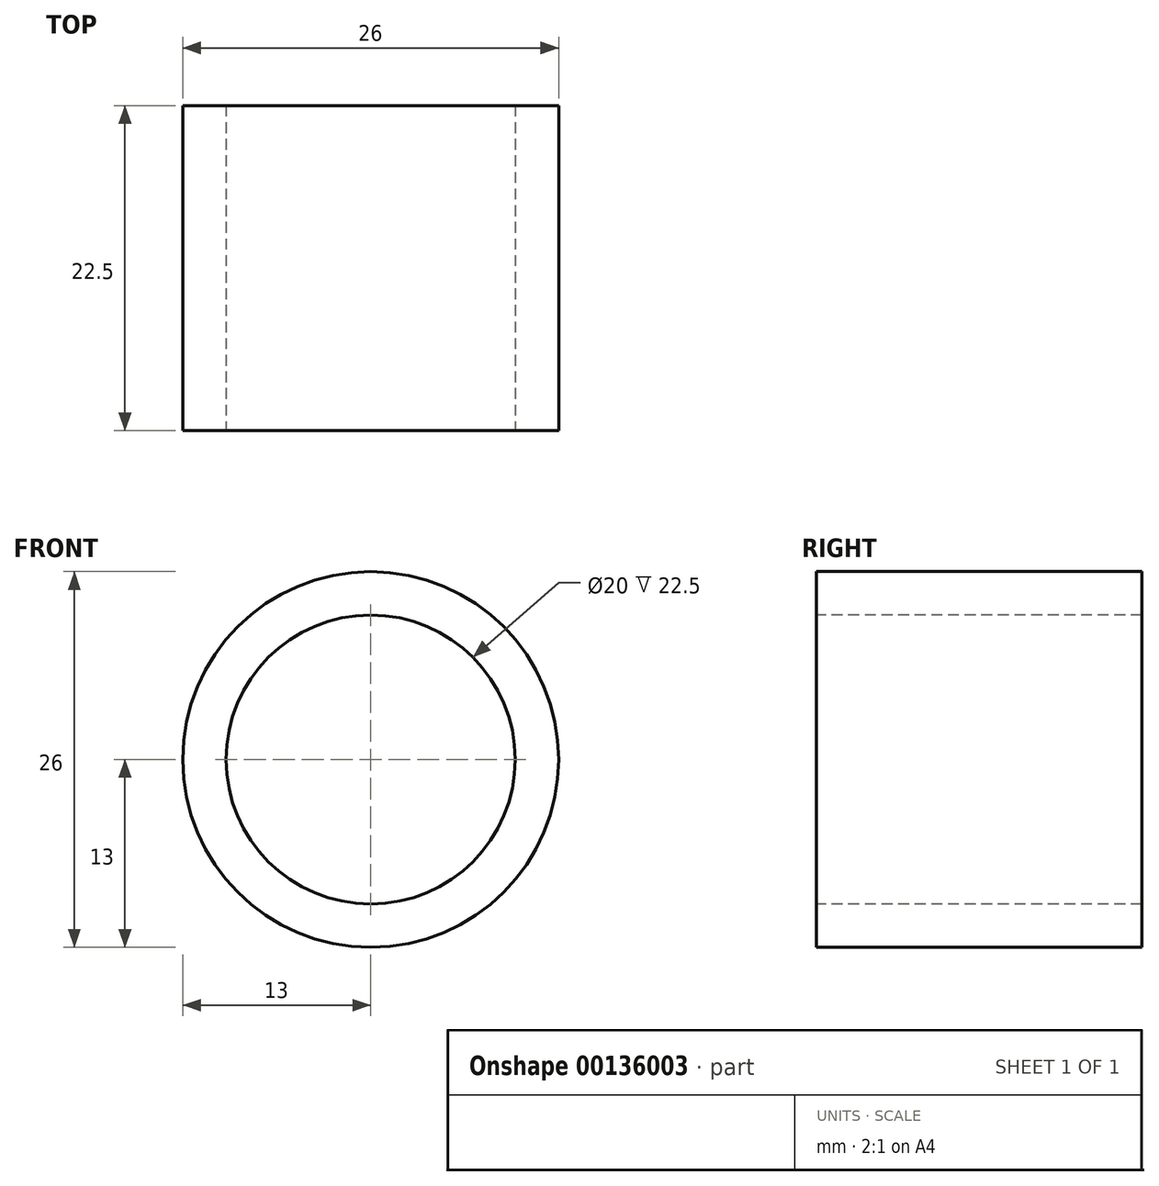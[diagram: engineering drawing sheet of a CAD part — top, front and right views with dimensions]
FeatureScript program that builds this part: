
annotation { "Feature Type Name" : "Feature", "Feature Type Description" : "" }
export const myFeature = defineFeature(function(context is Context, id is Id, definition is map)
    precondition{}
    {
        {
            var Q0;
            Q0=qCreatedBy(makeId("Front.planeOp"),FACE);
            var sketch = newSketch(context, id + "F0", { "sketchPlane" : qUnion([Q0])});
            skCircle(sketch, "E0", {"center": v(0, 0) * mm, "radius": 10 * mm});
            skCircle(sketch, "E1", {"center": v(0, 0) * mm, "radius": 13 * mm});
            skSolve(sketch);
        }
        {
            var Q0;
            Q0 = qSketchRegion(id + "F0", true);
            extrude(context, id + "F1", {"entities" : qUnion([Q0]), "oppositeDirection" : true, "depth" : 22.5 * mm});
        }
    });
